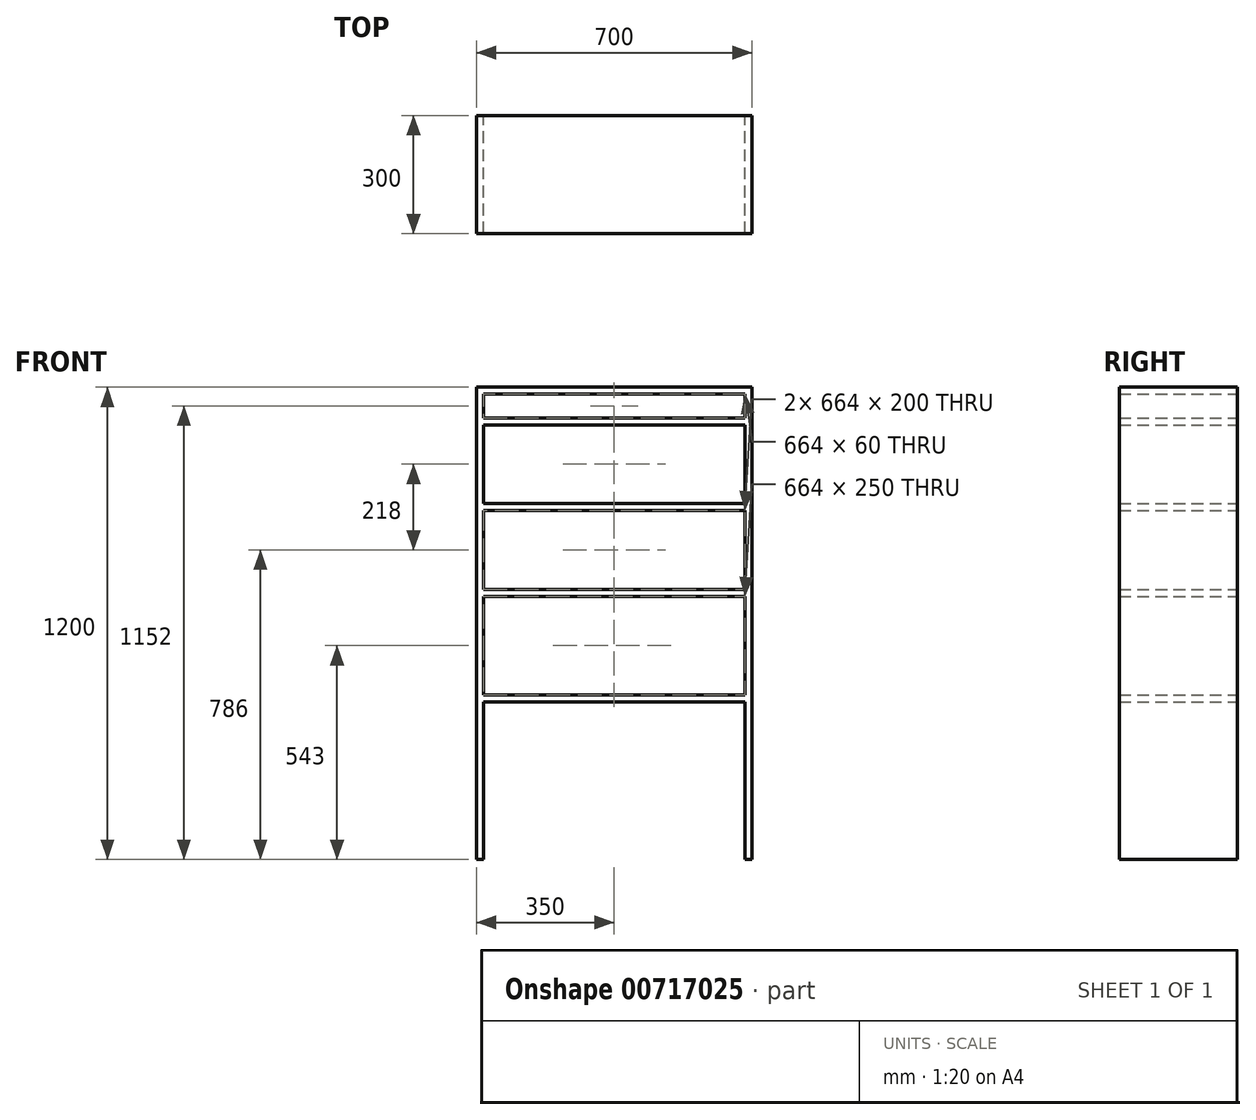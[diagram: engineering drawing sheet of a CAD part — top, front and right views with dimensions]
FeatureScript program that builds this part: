
annotation { "Feature Type Name" : "Feature", "Feature Type Description" : "" }
export const myFeature = defineFeature(function(context is Context, id is Id, definition is map)
    precondition{}
    {
        {
            var Q0;
            Q0=qCreatedBy(makeId("Front.planeOp"),FACE);
            var sketch = newSketch(context, id + "F0", { "sketchPlane" : qUnion([Q0])});
            skLineSegment(sketch, "E0.bottom", {"start": v(0, 0) * mm, "end": v(18, 0) * mm});
            skLineSegment(sketch, "E0.top", {"start": v(0, 1200) * mm, "end": v(18, 1200) * mm});
            skLineSegment(sketch, "E0.left", {"start": v(0, 0) * mm, "end": v(0, 1200) * mm});
            skLineSegment(sketch, "E0.right", {"start": v(18, 0) * mm, "end": v(18, 400) * mm});
            skLineSegment(sketch, "E1.bottom", {"start": v(682, 0) * mm, "end": v(700, 0) * mm});
            skLineSegment(sketch, "E1.top", {"start": v(682, 1200) * mm, "end": v(700, 1200) * mm});
            skLineSegment(sketch, "E1.left", {"start": v(682, 0) * mm, "end": v(682, 400) * mm});
            skLineSegment(sketch, "E1.right", {"start": v(700, 0) * mm, "end": v(700, 1200) * mm});
            skLineSegment(sketch, "E2.bottom", {"start": v(18, 418) * mm, "end": v(682, 418) * mm});
            skLineSegment(sketch, "E2.top", {"start": v(18, 400) * mm, "end": v(682, 400) * mm});
            skLineSegment(sketch, "E3.bottom", {"start": v(18, 668) * mm, "end": v(682, 668) * mm});
            skLineSegment(sketch, "E3.top", {"start": v(18, 686) * mm, "end": v(682, 686) * mm});
            skLineSegment(sketch, "E4.bottom", {"start": v(18, 886) * mm, "end": v(682, 886) * mm});
            skLineSegment(sketch, "E4.top", {"start": v(18, 904) * mm, "end": v(682, 904) * mm});
            skLineSegment(sketch, "E5.bottom", {"start": v(18, 1104) * mm, "end": v(682, 1104) * mm});
            skLineSegment(sketch, "E5.top", {"start": v(18, 1122) * mm, "end": v(682, 1122) * mm});
            skLineSegment(sketch, "E6.bottom", {"start": v(18, 1200) * mm, "end": v(682, 1200) * mm});
            skLineSegment(sketch, "E6.top", {"start": v(18, 1182) * mm, "end": v(682, 1182) * mm});
            skLineSegment(sketch, "E7.trimOffspring", {"start": v(18, 1122) * mm, "end": v(18, 1182) * mm});
            skLineSegment(sketch, "E8.trimOffspring", {"start": v(682, 1122) * mm, "end": v(682, 1182) * mm});
            skLineSegment(sketch, "E9.trimOffspring", {"start": v(18, 904) * mm, "end": v(18, 1104) * mm});
            skLineSegment(sketch, "E10.trimOffspring", {"start": v(682, 904) * mm, "end": v(682, 1104) * mm});
            skLineSegment(sketch, "E11.trimOffspring", {"start": v(18, 686) * mm, "end": v(18, 886) * mm});
            skLineSegment(sketch, "E12.trimOffspring", {"start": v(682, 686) * mm, "end": v(682, 886) * mm});
            skLineSegment(sketch, "E13.trimOffspring", {"start": v(682, 418) * mm, "end": v(682, 668) * mm});
            skLineSegment(sketch, "E14.trimOffspring", {"start": v(18, 418) * mm, "end": v(18, 668) * mm});
            skSolve(sketch);
        }
        {
            var Q0;
            Q0=makeQuery(id+"F0.imprint","IMPRINT",FACE,{"disambiguationData":[TD([[makeQuery(id+"F0.imprint","IMPRINT",EDGE,{"derivedFrom":sQuery(id+"F0.wireOp",EDGE,"E0.bottom")}),1.0]])]});
            extrude(context, id + "F1", {"entities" : qUnion([Q0]), "depth" : 300 * mm, "offsetDistance" : 25 * mm});
        }
    });
